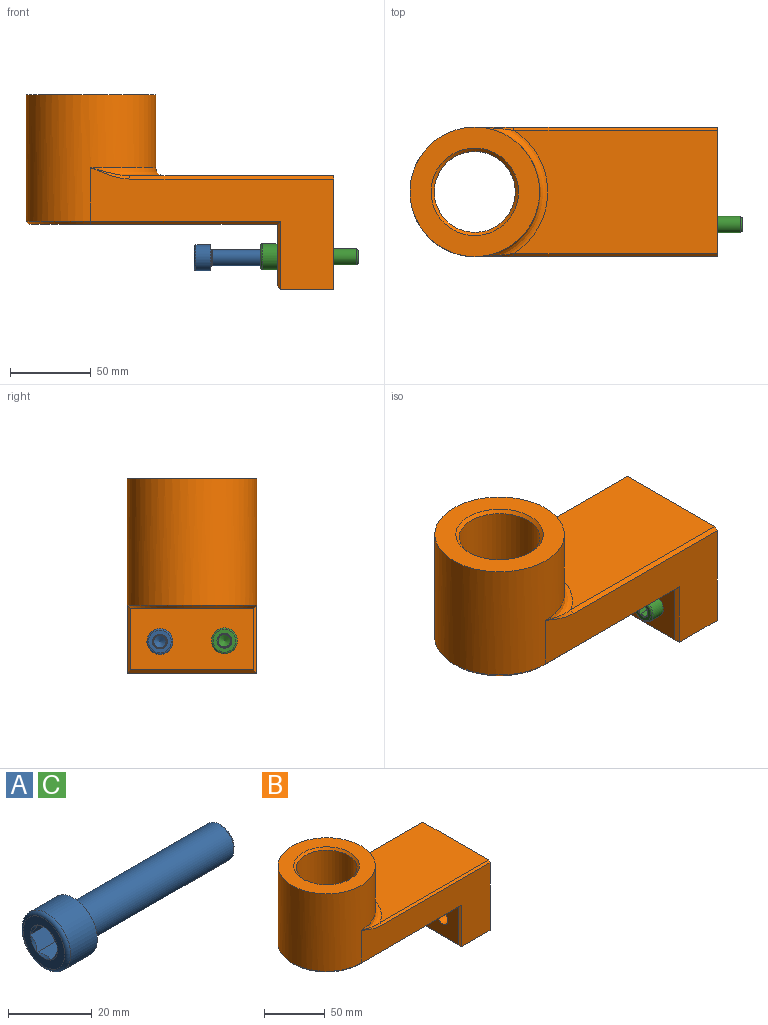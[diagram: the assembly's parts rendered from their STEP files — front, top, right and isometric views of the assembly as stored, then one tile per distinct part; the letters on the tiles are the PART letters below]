
ASSEMBLY  parts=3 mates=1
PART A: 24 faces, bbox 60x17.3x17.3 mm
  f0: cone r=1.9mm half-angle=60deg, axis (-1,0,0), area 52.6mm2, adj f16
  f1: torus R=7mm, axis (-1,0,0), area 75.4mm2, adj f2,f17
  f2: cylinder r=8mm len=16mm, axis (-1,0,0), area 452.4mm2, adj f1,f22
  f3: torus R=5.6mm, axis (-1,0,0), area 17mm2, adj f4,f22
  f4: cone r=5.12mm half-angle=17.9deg, axis (-1,0,0), area 21mm2, adj f3,f5
  f5: torus R=5.4mm, axis (-1,0,0), area 3.9mm2, adj f4,f6
  f6: cylinder r=5mm len=48.06mm, axis (-1,0,0), area 1509.8mm2, adj f5,f7
  f7: cone r=4.54mm half-angle=45deg, axis (-1,0,0), area 37.1mm2, adj f6,f21
  f8: cone r=4.19mm half-angle=45deg, axis (-1,0,0), area 2.4mm2, adj f15,f17
  f9: cone r=4.19mm half-angle=45deg, axis (-1,0,0), area 2.4mm2, adj f10,f17
  f10: plane 6x4.62mm, normal (0,0,1), area 26mm2, adj f9,f11,f14,f16,f17
  f11: plane 6x4mm, normal (0,-0.87,0.5), area 26mm2, adj f10,f12,f16,f17,f18
  f12: plane 6x4mm, normal (0,-0.87,-0.5), area 26mm2, adj f11,f15,f16,f17,f19
  f13: plane 6x4mm, normal (0,0.87,-0.5), area 26mm2, adj f14,f15,f16,f17,f20
  f14: plane 6x4mm, normal (0,0.87,0.5), area 26mm2, adj f10,f13,f16,f17,f23
  f15: plane 6x4.62mm, normal (0,0,-1), area 26mm2, adj f8,f12,f13,f16,f17
  f16: plane 9.24x8mm, normal (-1,0,0), area 9.8mm2, adj f0,f10,f11,f12,f13,f14,f15
  f17: plane 14x14mm, normal (-1,0,0), area 88.2mm2, adj f1,f8,f9,f10,f11,f12,f13,f14
  f18: cone r=4.19mm half-angle=45deg, axis (-1,0,0), area 2.4mm2, adj f11,f17
  f19: cone r=4.19mm half-angle=45deg, axis (-1,0,0), area 2.4mm2, adj f12,f17
  f20: cone r=4.19mm half-angle=45deg, axis (-1,0,0), area 2.4mm2, adj f13,f17
  f21: plane 8.16x8.16mm, normal (1,0,0), area 52.3mm2, adj f7
  f22: plane 16x16mm, normal (1,0,0), area 102.5mm2, adj f2,f3
  f23: cone r=4.19mm half-angle=45deg, axis (-1,0,0), area 2.4mm2, adj f14,f17
PART B: 25 faces, bbox 191.2x106.3x121.2 mm
  f0: plane 151.23x76.23mm, normal (0,1,0), area 5350mm2, adj f1,f3,f9,f16,f18,f21,f22
  f1: cylinder r=40mm len=80mm, axis (0,0,1), area 15456.6mm2, adj f0,f2,f7,f12,f20
  f2: plane 151.23x76.23mm, normal (0,-1,0), area 5350mm2, adj f1,f3,f9,f17,f19,f23,f24
  f3: plane 80x70mm, normal (1,0,0), area 5369.8mm2, adj f0,f2,f6,f8,f9,f10,f21,f23
  f4: cylinder r=25mm len=76mm, axis (0,0,1), area 11938.1mm2, adj f13,f14
  f5: plane 153x76mm, normal (0,0,-1), area 8718mm2, adj f11,f14,f18,f19,f20
  f6: plane 125.9x76mm, normal (0,0,1), area 8447.9mm2, adj f3,f12,f21,f23
  f7: plane 80x80mm, normal (0,0,1), area 2736.3mm2, adj f1,f13
  f8: cylinder r=6mm len=35mm, axis (1,0,0), area 1319.5mm2, adj f3,f11
  f9: plane 80x33mm, normal (0,0,-1), area 2640mm2, adj f0,f2,f3,f15
  f10: cylinder r=6mm len=35mm, axis (1,0,0), area 1319.5mm2, adj f3,f11
  f11: plane 76x38mm, normal (-1,0,0), area 2661.8mm2, adj f5,f8,f10,f15,f16,f17
  f12: torus R=45mm, axis (0,0,1), area 842.3mm2, adj f1,f6,f22,f24
  f13: cone r=25mm half-angle=45deg, axis (0,0,1), area 462.1mm2, adj f4,f7
  f14: cone r=27mm half-angle=45deg, axis (0,0,-1), area 462.1mm2, adj f4,f5
  f15: plane 80x2mm, normal (-0.71,0,-0.71), area 220.6mm2, adj f9,f11,f16,f17
  f16: plane 42x2mm, normal (-0.71,0.71,0), area 113.1mm2, adj f0,f11,f15,f18
  f17: plane 42x2mm, normal (-0.71,-0.71,0), area 113.1mm2, adj f2,f11,f15,f19
  f18: plane 117x2mm, normal (0,0.71,-0.71), area 328.1mm2, adj f0,f5,f16,f20
  f19: plane 117x2mm, normal (0,-0.71,-0.71), area 328.1mm2, adj f2,f5,f17,f20
  f20: cone r=40mm half-angle=45deg, axis (0,0,1), area 346.5mm2, adj f1,f5,f18,f19
  f21: plane 125.9x2mm, normal (0,0.71,0.71), area 356.1mm2, adj f0,f3,f6,f22
  f22: bspline ~24.1x7.1mm, area 24.3mm2, adj f0,f12,f21
  f23: plane 125.9x2mm, normal (0,-0.71,0.71), area 356.1mm2, adj f2,f3,f6,f24
  f24: bspline ~24.1x7.1mm, area 24.3mm2, adj f2,f12,f23
PART C: same geometry as A
PLACE A t=(-1.06,19.82,-50.48)mm
PLACE B at identity
PLACE C t=(39.95,-20,-50)mm
MATE cylindrical C.f0 <-> B.f8  axis (-1,0,0) through (65,-20,-50)mm
